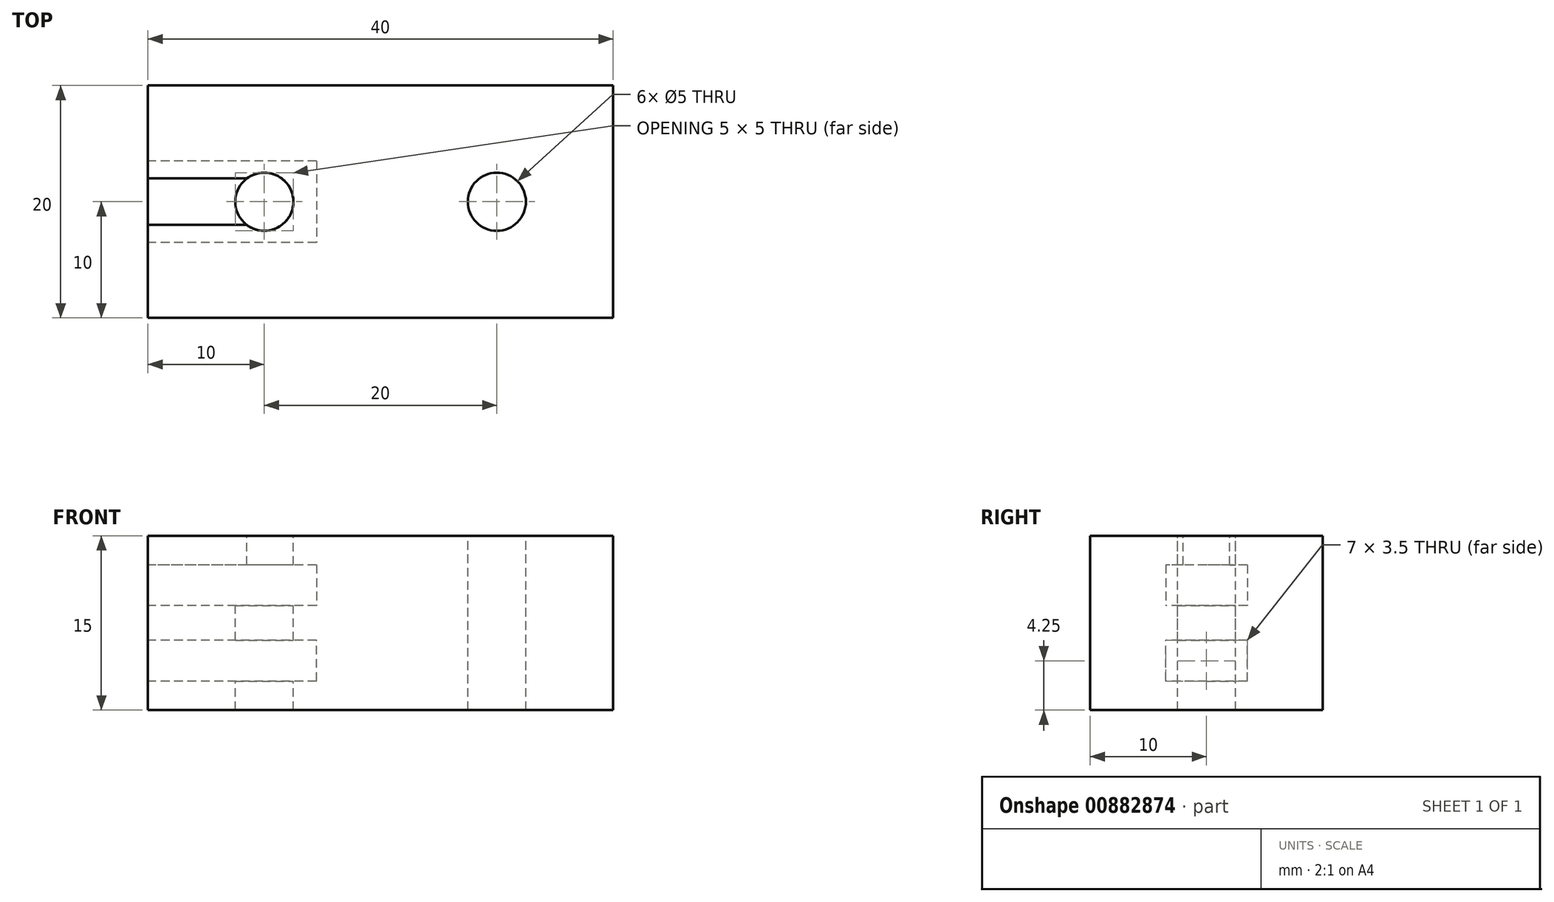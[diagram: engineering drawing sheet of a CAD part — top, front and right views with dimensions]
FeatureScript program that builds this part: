
annotation { "Feature Type Name" : "Feature", "Feature Type Description" : "" }
export const myFeature = defineFeature(function(context is Context, id is Id, definition is map)
    precondition{}
    {
        {
            var Q0;
            Q0=qCreatedBy(makeId("Top.planeOp"),FACE);
            var sketch = newSketch(context, id + "F0", { "sketchPlane" : qUnion([Q0])});
            skLineSegment(sketch, "E0.bottom", {"start": v(20, -10) * mm, "end": v(-20, -10) * mm});
            skLineSegment(sketch, "E0.top", {"start": v(20, 10) * mm, "end": v(-20, 10) * mm});
            skLineSegment(sketch, "E0.left", {"start": v(20, -10) * mm, "end": v(20, 10) * mm});
            skLineSegment(sketch, "E0.right", {"start": v(-20, -10) * mm, "end": v(-20, 10) * mm});
            skPoint(sketch, "E0.middle", {"position": v(0, 0) * mm});
            skSolve(sketch);
        }
        {
            var Q0;
            Q0=qSketchRegion(id+"F0",true);
            extrude(context, id + "F1", {"entities" : qUnion([Q0]), "depth" : 15 * mm, "offsetDistance" : 25 * mm});
        }
        {
            var Q0;
            Q0=makeQuery(id+"F1.opExtrude","CAP_FACE",FACE,{"disambiguationData":[OSD([sQuery(id+"F0.wireOp",EDGE,"E0.bottom"),sQuery(id+"F0.wireOp",EDGE,"E0.top"),sQuery(id+"F0.wireOp",EDGE,"E0.left"),sQuery(id+"F0.wireOp",EDGE,"E0.right")])],"isStart":false});
            var sketch = newSketch(context, id + "F2", { "sketchPlane" : qUnion([Q0])});
            skCircle(sketch, "E1", {"center": v(-10, 0) * mm, "radius": 2.5 * mm});
            skCircle(sketch, "E2.MirrorC", {"center": v(10, 0) * mm, "radius": 2.5 * mm});
            skLineSegment(sketch, "E3", {"start": v(-29.23, 0) * mm, "end": v(9.23, 0) * mm, "construction": true});
            skSolve(sketch);
        }
        {
            var Q0;
            Q0=qSketchRegion(id+"F2",true);
            extrude(context, id + "F3", {"entities" : qUnion([Q0]), "operationType" : NewBodyOperationType.REMOVE, "endBound" : BoundingType.THROUGH_ALL, "oppositeDirection" : true, "depth" : 25 * mm, "offsetDistance" : 25 * mm});
        }
        {
            var Q0;
            Q0=makeQuery(id+"F1.opExtrude","SWEPT_FACE",FACE,{"disambiguationData":[OSD([sQuery(id+"F0.wireOp",EDGE,"E0.right")])]});
            var sketch = newSketch(context, id + "F4", { "sketchPlane" : qUnion([Q0])});
            skLineSegment(sketch, "E4.bottom", {"start": v(-3.5, 2.5) * mm, "end": v(3.5, 2.5) * mm});
            skLineSegment(sketch, "E4.top", {"start": v(-3.5, 6) * mm, "end": v(3.5, 6) * mm});
            skLineSegment(sketch, "E4.left", {"start": v(-3.5, 2.5) * mm, "end": v(-3.5, 6) * mm});
            skLineSegment(sketch, "E4.right", {"start": v(3.5, 2.5) * mm, "end": v(3.5, 6) * mm});
            skLineSegment(sketch, "E5", {"start": v(-15.4, 7.5) * mm, "end": v(18.42, 7.5) * mm, "construction": true});
            skLineSegment(sketch, "E6.MirrorCS", {"start": v(-3.5, 9) * mm, "end": v(3.5, 9) * mm});
            skLineSegment(sketch, "E7.MirrorCS", {"start": v(-3.5, 12.5) * mm, "end": v(-3.5, 9) * mm});
            skLineSegment(sketch, "E8.MirrorCS", {"start": v(-3.5, 12.5) * mm, "end": v(3.5, 12.5) * mm});
            skLineSegment(sketch, "E9.MirrorCS", {"start": v(3.5, 12.5) * mm, "end": v(3.5, 9) * mm});
            skSolve(sketch);
        }
        {
            var Q0;
            Q0 = qSketchRegion(id + "F4", true);
            extrude(context, id + "F5", {"entities" : qUnion([Q0]), "operationType" : NewBodyOperationType.REMOVE, "oppositeDirection" : true, "depth" : 14.5 * mm, "offsetDistance" : 25 * mm});
        }
        {
            var Q0;
            Q0=makeQuery(id+"F1.opExtrude","SWEPT_FACE",FACE,{"disambiguationData":[OSD([sQuery(id+"F0.wireOp",EDGE,"E0.right")])]});
            var sketch = newSketch(context, id + "F6", { "sketchPlane" : qUnion([Q0])});
            skLineSegment(sketch, "E10.bottom", {"start": v(-2, 15) * mm, "end": v(2, 15) * mm});
            skLineSegment(sketch, "E10.top", {"start": v(-2, 12.5) * mm, "end": v(2, 12.5) * mm});
            skLineSegment(sketch, "E10.left", {"start": v(-2, 15) * mm, "end": v(-2, 12.5) * mm});
            skLineSegment(sketch, "E10.right", {"start": v(2, 15) * mm, "end": v(2, 12.5) * mm});
            skSolve(sketch);
        }
        {
            var Q0;
            Q0 = qSketchRegion(id + "F6", true);
            extrude(context, id + "F7", {"entities" : qUnion([Q0]), "operationType" : NewBodyOperationType.REMOVE, "oppositeDirection" : true, "depth" : 12.5 * mm, "offsetDistance" : 25 * mm});
        }
        {
            var Q0;
            Q0=makeQuery(id+"F7.boolean.opBoolean","COPY",EDGE,{"derivedFrom":makeQuery(id+"F7.opExtrude","CAP_EDGE",EDGE,{"disambiguationData":[OSD([sQuery(id+"F6.wireOp",EDGE,"E10.right")])],"isStart":false})});
            fillet(context, id + "F8", {"entities" : qUnion([Q0]), "radius" : 2.5 * mm, "tangentPropagation" : true, "allowEdgeOverflow" : false});
        }
        {
            var Q0;
            Q0=makeQuery(id+"F7.boolean.opBoolean","COPY",EDGE,{"derivedFrom":makeQuery(id+"F7.opExtrude","CAP_EDGE",EDGE,{"disambiguationData":[OSD([sQuery(id+"F6.wireOp",EDGE,"E10.left")])],"isStart":false})});
            fillet(context, id + "F9", {"entities" : qUnion([Q0]), "radius" : 2.5 * mm, "tangentPropagation" : true, "allowEdgeOverflow" : false});
        }
    });
